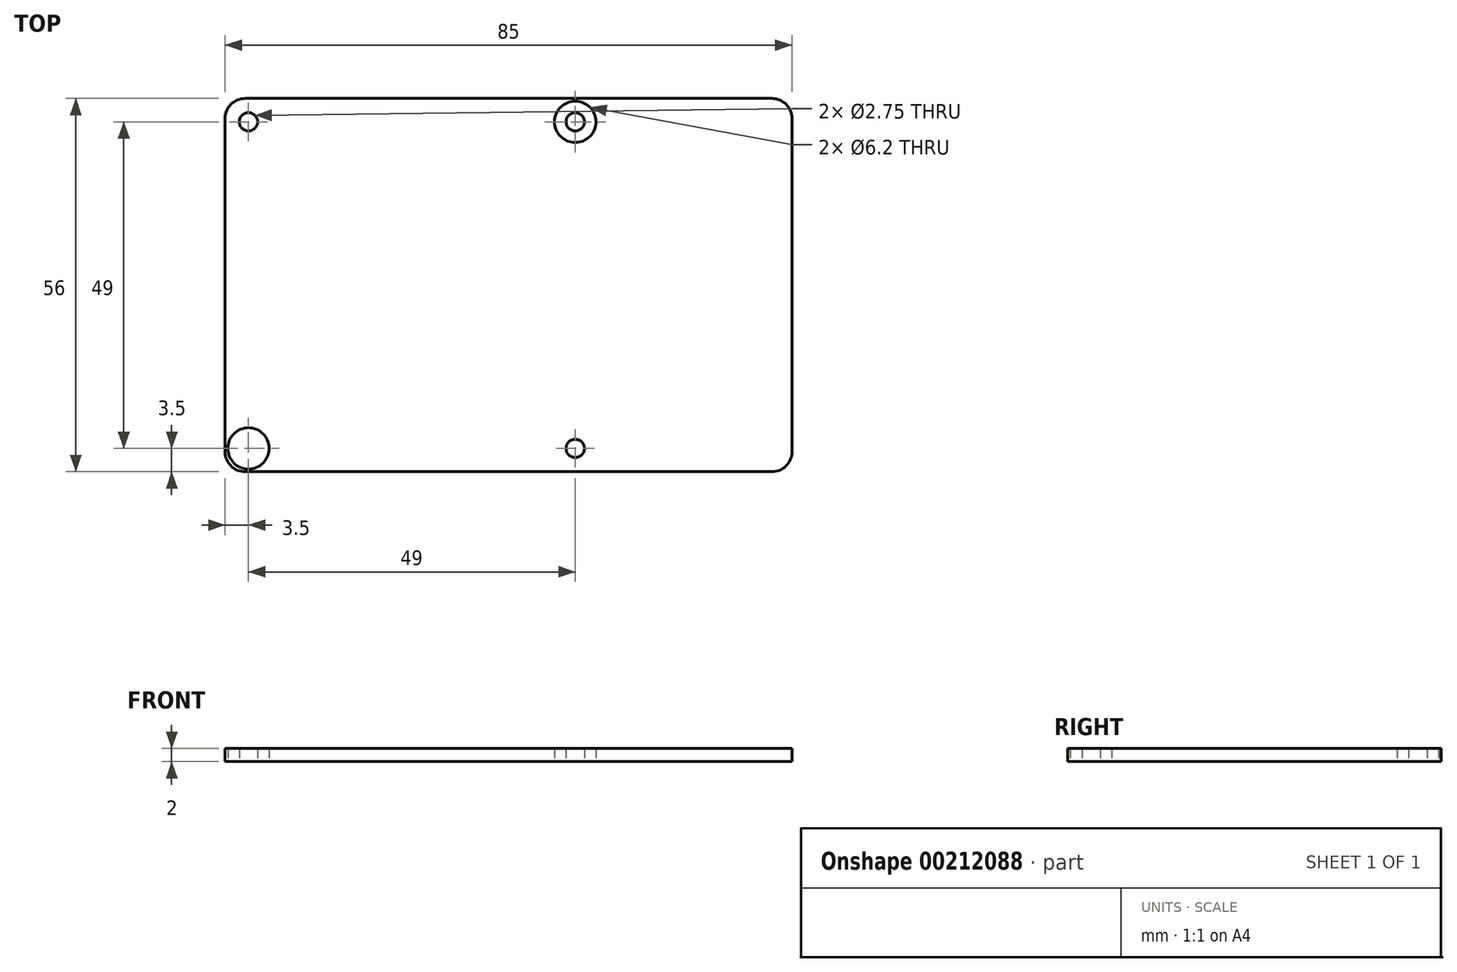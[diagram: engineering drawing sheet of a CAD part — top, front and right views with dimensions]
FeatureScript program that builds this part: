
annotation { "Feature Type Name" : "Feature", "Feature Type Description" : "" }
export const myFeature = defineFeature(function(context is Context, id is Id, definition is map)
    precondition{}
    {
        {
            var Q0;
            Q0=qCreatedBy(makeId("Top.planeOp"),FACE);
            var sketch = newSketch(context, id + "F0", { "sketchPlane" : qUnion([Q0])});
            skLineSegment(sketch, "E0.bottom", {"start": v(-39.5, 28) * mm, "end": v(39.5, 28) * mm});
            skLineSegment(sketch, "E0.top", {"start": v(-39.5, -28) * mm, "end": v(39.5, -28) * mm});
            skLineSegment(sketch, "E0.left", {"start": v(-42.5, 25) * mm, "end": v(-42.5, -25) * mm});
            skLineSegment(sketch, "E0.right", {"start": v(42.5, 25) * mm, "end": v(42.5, -25) * mm});
            skPoint(sketch, "E0.middle", {"position": v(0, 0) * mm});
            skPoint(sketch, "E1.visualSharp", {"position": v(-42.5, 28) * mm});
            skArc(sketch, "E1.filletArc", {"start": v(-39.5, 28) * mm, "mid": v(-41.62, 27.12) * mm, "end": v(-42.5, 25) * mm});
            skPoint(sketch, "E2.visualSharp", {"position": v(42.5, 28) * mm});
            skArc(sketch, "E2.filletArc", {"start": v(42.5, 25) * mm, "mid": v(41.62, 27.12) * mm, "end": v(39.5, 28) * mm});
            skPoint(sketch, "E3.visualSharp", {"position": v(42.5, -28) * mm});
            skArc(sketch, "E3.filletArc", {"start": v(39.5, -28) * mm, "mid": v(41.62, -27.12) * mm, "end": v(42.5, -25) * mm});
            skPoint(sketch, "E4.visualSharp", {"position": v(-42.5, -28) * mm});
            skArc(sketch, "E4.filletArc", {"start": v(-42.5, -25) * mm, "mid": v(-41.62, -27.12) * mm, "end": v(-39.5, -28) * mm});
            skCircle(sketch, "E5", {"center": v(-39, 24.5) * mm, "radius": 1.38 * mm});
            skCircle(sketch, "E6", {"center": v(-39, 24.5) * mm, "radius": 3.1 * mm});
            skCircle(sketch, "E7.MirrorC", {"center": v(-39, -24.5) * mm, "radius": 3.1 * mm});
            skCircle(sketch, "E8.MirrorC", {"center": v(-39, -24.5) * mm, "radius": 1.38 * mm});
            skLineSegment(sketch, "E9", {"start": v(-14.5, 28) * mm, "end": v(-14.5, -28) * mm, "construction": true});
            skCircle(sketch, "E10.MirrorC", {"center": v(10, 24.5) * mm, "radius": 1.38 * mm});
            skCircle(sketch, "E11.MirrorC", {"center": v(10, 24.5) * mm, "radius": 3.1 * mm});
            skCircle(sketch, "E12.MirrorC", {"center": v(10, -24.5) * mm, "radius": 3.1 * mm});
            skCircle(sketch, "E13.MirrorC", {"center": v(10, -24.5) * mm, "radius": 1.38 * mm});
            skSolve(sketch);
        }
        {
            var Q0;
            Q0=makeQuery(id+"F0.imprint","IMPRINT",FACE,{"disambiguationData":[TD([[makeQuery(id+"F0.imprint","IMPRINT",EDGE,{"derivedFrom":sQuery(id+"F0.wireOp",EDGE,"E0.bottom")}),-1.0]])]});
            var Q1;
            Q1=makeQuery(id+"F0.imprint","IMPRINT",FACE,{"disambiguationData":[TD([[makeQuery(id+"F0.imprint","IMPRINT",EDGE,{"derivedFrom":sQuery(id+"F0.wireOp",EDGE,"E10.MirrorC")}),1.0]])]});
            var Q2;
            Q2=makeQuery(id+"F0.imprint","IMPRINT",FACE,{"disambiguationData":[TD([[makeQuery(id+"F0.imprint","IMPRINT",EDGE,{"derivedFrom":sQuery(id+"F0.wireOp",EDGE,"E12.MirrorC")}),1.0]])]});
            var Q3;
            Q3=makeQuery(id+"F0.imprint","IMPRINT",FACE,{"disambiguationData":[TD([[makeQuery(id+"F0.imprint","IMPRINT",EDGE,{"derivedFrom":sQuery(id+"F0.wireOp",EDGE,"E7.MirrorC")}),-1.0]])]});
            var Q4;
            Q4=makeQuery(id+"F0.imprint","IMPRINT",FACE,{"disambiguationData":[TD([[makeQuery(id+"F0.imprint","IMPRINT",EDGE,{"derivedFrom":sQuery(id+"F0.wireOp",EDGE,"E5")}),-1.0]])]});
            extrude(context, id + "F1", {"entities" : qUnion([Q0, Q1, Q2, Q3, Q4]), "depth" : 2 * mm});
        }
    });
